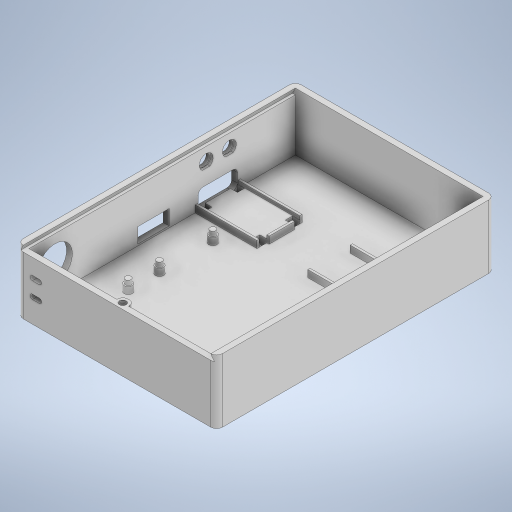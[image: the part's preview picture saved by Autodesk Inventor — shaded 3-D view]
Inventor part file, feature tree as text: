
AUTODESK INVENTOR PART (.ipt)
format: ipt  version: 2023 (Build 270158000, 158)  size: 824,320 bytes
history: native  units: mm
features: extrude x23, sketch x21, fillet x2, plane x2, thread x1, projected_geometry x1
ambient origin geometry x8: Origin, YZ Plane, XZ Plane, XY Plane, X Axis, Y Axis, Z Axis, Center Point
bodies: Solid1 (feature_tree)
feature tree (50):
  sketch  "Sketch1"  dims[d0=76.0mm d1=20.0mm]
  extrude  "Extrusion3"  Depth=20.0mm
  extrude  "Extrusion12"  Depth=5.0mm
  fillet  "Fillet6"  [1 undecoded]
  extrude  "Extrusion1"  Depth=2.55mm
  extrude  "Extrusion13"  Depth=81.0mm
  extrude  "Extrusion14"  TaperAngle=0.0deg  [1 undecoded]
  extrude  "Extrusion15"  Depth=2.5mm
  plane  "Work Plane6"
  sketch  "Sketch13"  dims[d17=2.55mm d18=58.05mm d24=81.0mm]
  sketch  "Sketch14"  dims[d26=5.0mm d27=0.0mm d31=0.0mm]
  extrude  "Extrusion18"  Depth=2.5mm
  sketch  "Sketch16"  dims[d34=2.5mm d35=2.5mm d36=25.0mm d37=0.0mm]
  fillet  "Fillet7"  Radius=25.0mm
  sketch  "Sketch17"  dims[d72=17.0mm d73=28.662mm]
  extrude  "Extrusion19"  Depth=28.662mm
  sketch  "Sketch19"  dims[d76=3.0mm d77=3.0mm]
  extrude  "Extrusion21"  Depth=3.0mm
  extrude  "Extrusion22"  Depth=3.0mm
  plane  "Work Plane8"
  sketch  "Sketch22"  dims[d82=3.0mm d83=3.0mm]
  sketch  "Sketch24"  dims[d102=2.5mm d103=0.0mm d104=2.5mm]
  extrude  "Extrusion23"  Depth=2.0mm
  extrude  "Extrusion24"  Depth=3.0mm
  extrude  "Extrusion25"  Depth=3.0mm
  extrude  "Extrusion26"  Depth=2.5mm
  extrude  "Extrusion27"  Depth=3.55mm
  extrude  "Extrusion28"  Depth=3.55mm
  extrude  "Extrusion29"  Depth=3.0mm TaperAngle=0.0deg
  extrude  "Extrusion30"  Depth=30.0mm
  extrude  "Extrusion31"  Depth=5.0mm
  thread  "Thread2"  [1 undecoded]
  extrude  "Extrusion32"  Depth=2.0mm
  extrude  "Extrusion33"  Depth=0.25mm
  extrude  "Extrusion34"  Depth=0.25mm
  extrude  "Extrusion35"  Depth=0.25mm
  sketch  "Sketch11"  dims[d2=38.0mm d4=5.0mm d5=0.0mm]
  sketch  "Sketch12"  dims[d14=2.55mm d15=2.55mm]
  sketch  "Sketch15"  dims[d32=2.5mm d33=2.5mm]
  sketch  "Sketch18"  dims[d74=28.662mm d75=3.0mm]
  sketch  "Sketch20"  dims[d78=3.0mm d79=2.0mm]
  sketch  "Sketch21"  dims[d80=3.0mm d81=3.0mm]
  sketch  "Sketch25"  dims[d105=3.55mm d106=3.55mm]
  sketch  "Sketch26"  dims[d107=3.55mm d108=3.55mm]
  sketch  "Sketch29"  dims[d109=2.55mm d110=3.0mm d111=0.0mm]
  sketch  "Sketch33"  dims[d115=65.0mm d116=30.0mm]
  sketch  "Sketch34"  dims[d119=5.0mm d120=5.0mm d122=2.0mm d123=0.0mm]
  sketch  "Sketch35"  dims[d124=8.0mm d125=2.0mm]
  sketch  "Sketch36"  dims[d126=0.0mm d127=0.0mm d128=5.0mm d129=5.0mm d130=5.0mm d131=5.0mm d132=6.0mm d133=6.0mm d138=5.0mm d139=2.0mm d140=2.0mm d141=5.0mm d143=5.0mm d144=3.0mm d145=1.5mm d146=0.0mm d147=1.0mm d150=6.5mm d151=13.5mm d152=8.0mm d156=10.0mm d157=0.0mm d160=13.5mm d166=15.0mm d167=13.75mm d168=13.75mm d169=10.0mm d170=0.0mm d172=27.5mm d174=27.5mm d175=9.0mm d176=9.25mm d180=2.5mm d181=2.5mm d182=1.25mm d183=1.25mm d184=10.0mm d185=0.0mm d186=5.0mm d188=5.0mm d189=17.5mm d191=1.25mm d192=2.0mm d195=2.5mm d196=0.75mm d197=2.55mm d198=13.5mm d199=3.55mm d200=14.862858mm d201=14.862858mm d202=36.55mm d203=36.55mm d204=2.55mm d205=3.55mm d206=58.05mm d208=54.5mm d209=114.983311mm d210=119.983311mm d211=2.55mm d212=3.55mm d213=20.32mm d214=23.05mm d215=7.717142mm d216=5.0mm d217=0.0mm d218=3.0mm d219=0.0mm d221=5.0mm d222=2.5mm d224=0.0mm d225=2.0mm d226=3.0mm d227=0.0mm d229=3.0mm d230=0.0mm d231=0.0mm d234=10.0mm d235=0.0mm d236=1.0mm d237=0.0mm d238=1.5mm d239=0.0mm d240=1.0mm d241=3.0mm d242=0.0mm d243=21.0mm d244=90.0deg d245=1.0mm d246=0.0mm d248=58.42mm d252=38.0mm d253=38.0mm d254=81.0mm d257=5.0mm d258=2.5mm d259=9.0mm d260=0.0mm d261=12.5mm d263=0.456mm d264=0.456mm d265=2.0mm d266=0.0mm d267=2.5mm d268=5.0mm d270=3.087142mm d273=0.0mm d274=0.0mm d275=23.05mm d276=23.05mm d277=17.3mm d278=20.0mm d279=20.0mm d280=1.0mm d281=1.0mm d282=12.5mm d283=0.15mm d284=17.0mm d285=3.0mm d286=0.0mm d287=0.25mm d288=0.25mm d289=0.0mm d290=1.0mm d291=1.0mm d292=1.0mm d293=1.0mm d294=0.0mm d295=0.0mm d296=3.0mm d297=0.0mm d298=0.25mm d299=2.694788mm d300=1.222394mm d302=2.694788mm d303=1.222394mm d304=0.25mm d305=10.0mm d306=0.0mm d38=0.0mm d39=0.0mm d40=0.0mm d41=0.0mm d95=0.5mm d96=0.872665mm d97=0.5mm d98=0.872665mm d112=0.5mm d113=0.872665mm d114=0.5mm d193=0.872665mm d194=0.872665mm d307=0.5mm d308=0.872665mm]
  projected_geometry  "Projected Loop1"
note: 3 required parameter values undecoded (feature->parameter linkage not recoverable at this tier; creation-order binding heuristic only, values carry confidence <= 0.55)
